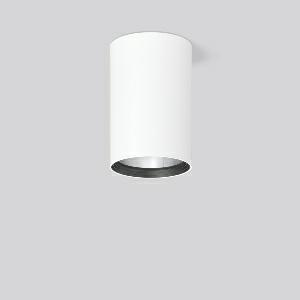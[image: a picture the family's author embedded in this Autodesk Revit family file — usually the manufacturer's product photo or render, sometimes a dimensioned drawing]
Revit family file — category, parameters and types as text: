
# Revit family: heledon_maxi_a_931246_002_2_76_2d0d
name_source: partatom
category: Lighting Fixtures
units: mm (PartAtom-declared; Revit-internal decimal feet)

## family parameters
Cut with Voids When Loaded = No
Host = Face
Light Source = No
Part Type = Normal
Room Calculation Point = No
Round Connector Dimension = Use Diameter
Shared = No

## types (1)
- HELEDON maxi A (1 x LED Modul 927 bakery, 3450 lm, 2700)
    Apparent Load = 33 VA
    Approval mark = CE
    CIE Flux Codes = 100 100 100 100 100
    Color Rendering = 90
    Color Temperature = 2700
    Default Elevation = 1800 mm
    Description = Series: HELEDON maxi
Cylindrical surface-mounted downlight. Housing: die-cast aluminium, powder-coated. Internal ceiling frame polycarbonate with bayonet mounting. Black plastic ring and recessed LED to prevent glare from the side. Optical assembly with reflector made of MIRO-Silver with 98% total light reflection for outstanding efficiency - can be changed without tools. Special LED for illumination of pastries included. Suitable for Ceiling mounting. Easy installation with a separate ceiling frame with bayonet mounting and plug connection. Driver integrated. Connected via plug-in connector. High quality converter without flickering and stroboscopic effect. The following accessories can be mounted without use of tools: interchangeable lenses, decorative glasses, honeycomb louvre, clear and frosted diffusers, white interchangeable plastic ring. 
Colour: traffic white, matt (RAL 9016)
Diameter: 123 mm
Height: 183 mm
Lamp: LED
Socket: without socket
Colour temperature: bakery
Colour rendering index (CRI): 97
System power: 33 W
Rated luminous flux: 3450 lm
Luminous efficiency: 105 lm/W
Control gear: Converter, dimmable, DALI
Protection class: I
Type of protection: IP 20
    Height = 183 mm
    Lamp = 1 x LED Modul 927 bakery
    Lamp Light Flux = 3450 lm
    Lamp count = 1
    Length = 123 mm
    Lifetime = 50000 h
    Luminous efficacy = 105 lm/W
    Manufacturer = RZB
    ModVariant = No
    Model = 931246.002.2.76
    Mounting Place = Ceiling
    Mounting Type = Surface mounted
    Number of Poles = 1
    OnlyDefault = Yes
    Power Factor = 1
    Product Name = HELEDON maxi A
    Product group = Surface mounted downlights
    ProductGroupID = 302
    Protection Class = Protection class I
    Protection Degree = IP 20
    RLX_Detail_Level = 1
    RLX_Emergency_Light_Flux = 0 lm
    RLX_Emergency_Type = 0
    RLX_Emergency_Type_DB = No
    RlxData = <blob elided: 98069 chars, md5=e540b1a9>
    Socket = socket
    Standby Power = 0 W
    System Light Flux = 3450 lm
    System Power = 33 W
    Type Comments = Product without accessories
    Type Image = 931192.002.jpg
    URL = http://relux.com
    VarID = ---
    Voltage = 230 V
    Voltage Range = 220-240 V
    Weight = 0.00 kg
    Width = 0 mm  [stored 0 ft]

note: [stored X ft] marks values corroborated as IEEE doubles in the binary element streams (Revit-internal decimal feet)

## geometry (parser evidence)
native form markers: Blend x4, Sweep x10
no freeform markers — native parametric forms only
